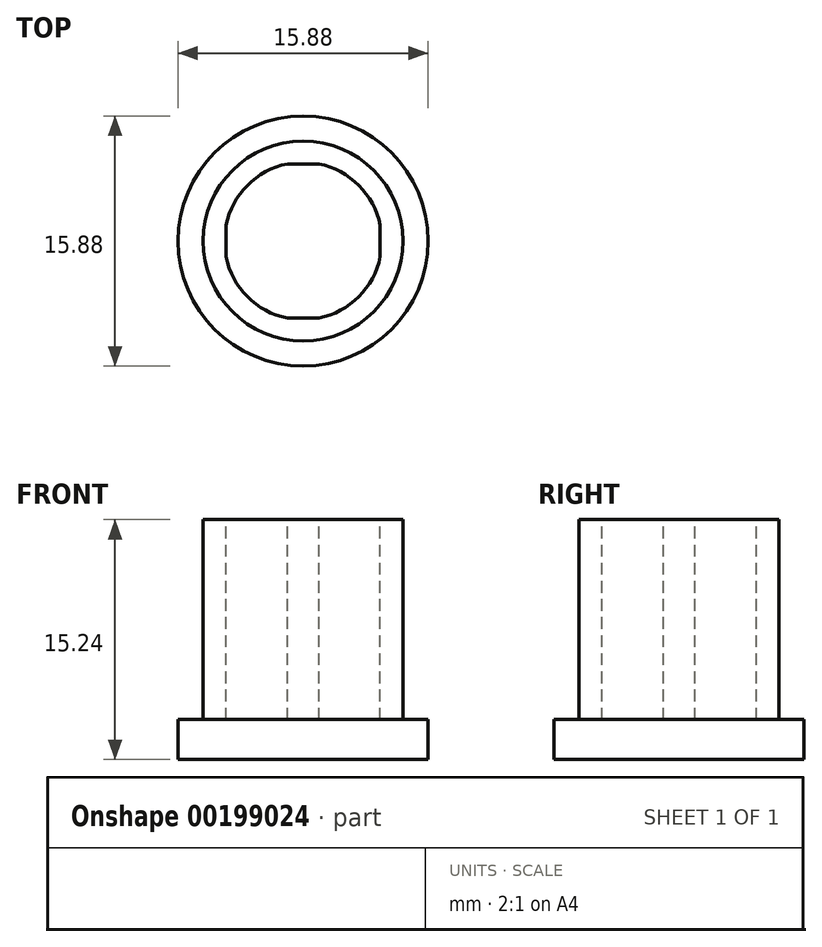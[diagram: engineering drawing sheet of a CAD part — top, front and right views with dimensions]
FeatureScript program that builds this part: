
annotation { "Feature Type Name" : "Feature", "Feature Type Description" : "" }
export const myFeature = defineFeature(function(context is Context, id is Id, definition is map)
    precondition{}
    {
        {
            var Q0;
            Q0=qCreatedBy(makeId("Top.planeOp"),FACE);
            var sketch = newSketch(context, id + "F0", { "sketchPlane" : qUnion([Q0])});
            skCircle(sketch, "E0", {"center": v(0, 0) * mm, "radius": 7.94 * mm});
            skSolve(sketch);
        }
        {
            var Q0;
            Q0 = qSketchRegion(id + "F0", true);
            extrude(context, id + "F1", {"entities" : qUnion([Q0]), "depth" : 2.54 * mm});
        }
        {
            var Q0;
            Q0=makeQuery(id+"F1.opExtrude","CAP_FACE",FACE,{"disambiguationData":[OSD([sQuery(id+"F0.wireOp",EDGE,"E0")])],"isStart":false});
            var sketch = newSketch(context, id + "F2", { "sketchPlane" : qUnion([Q0])});
            skCircle(sketch, "E1", {"center": v(0, 0) * mm, "radius": 6.35 * mm});
            skSolve(sketch);
        }
        {
            var Q0;
            Q0 = qSketchRegion(id + "F2", true);
            extrude(context, id + "F3", {"entities" : qUnion([Q0]), "operationType" : NewBodyOperationType.ADD, "depth" : 12.7 * mm});
        }
        {
            var Q0;
            Q0=makeQuery(id+"F3.opExtrude","CAP_FACE",FACE,{"disambiguationData":[OSD([sQuery(id+"F2.wireOp",EDGE,"E1")])],"isStart":false});
            var sketch = newSketch(context, id + "F4", { "sketchPlane" : qUnion([Q0])});
            skArc(sketch, "E2", {"start": v(-1, 4.9) * mm, "mid": v(-3.54, 3.54) * mm, "end": v(-4.9, 1) * mm});
            skLineSegment(sketch, "E3", {"start": v(-1, 4.9) * mm, "end": v(1, 4.9) * mm});
            skLineSegment(sketch, "E4.1.0", {"start": v(-4.9, -1) * mm, "end": v(-4.9, 1) * mm});
            skLineSegment(sketch, "E4.2.0", {"start": v(1, -4.9) * mm, "end": v(-1, -4.9) * mm});
            skArc(sketch, "E5.trimOffspring", {"start": v(-4.9, -1) * mm, "mid": v(-3.54, -3.54) * mm, "end": v(-1, -4.9) * mm});
            skArc(sketch, "E6.trimOffspring", {"start": v(4.9, 1) * mm, "mid": v(3.54, 3.54) * mm, "end": v(1, 4.9) * mm});
            skLineSegment(sketch, "E7.1.3.0", {"start": v(4.9, 1) * mm, "end": v(4.9, -1) * mm});
            skArc(sketch, "E8.trimOffspring", {"start": v(1, -4.9) * mm, "mid": v(3.54, -3.54) * mm, "end": v(4.9, -1) * mm});
            skSolve(sketch);
        }
        {
            var Q0;
            Q0 = qSketchRegion(id + "F4", true);
            var Q1;
            Q1=makeQuery(id+"F1.opExtrude","CAP_FACE",FACE,{"disambiguationData":[OSD([sQuery(id+"F0.wireOp",EDGE,"E0")])],"isStart":false});
            extrude(context, id + "F5", {"entities" : qUnion([Q0]), "operationType" : NewBodyOperationType.REMOVE, "endBound" : BoundingType.UP_TO_SURFACE, "oppositeDirection" : true, "endBoundEntityFace" : qUnion([Q1]), "depth" : 25.4 * mm});
        }
    });
